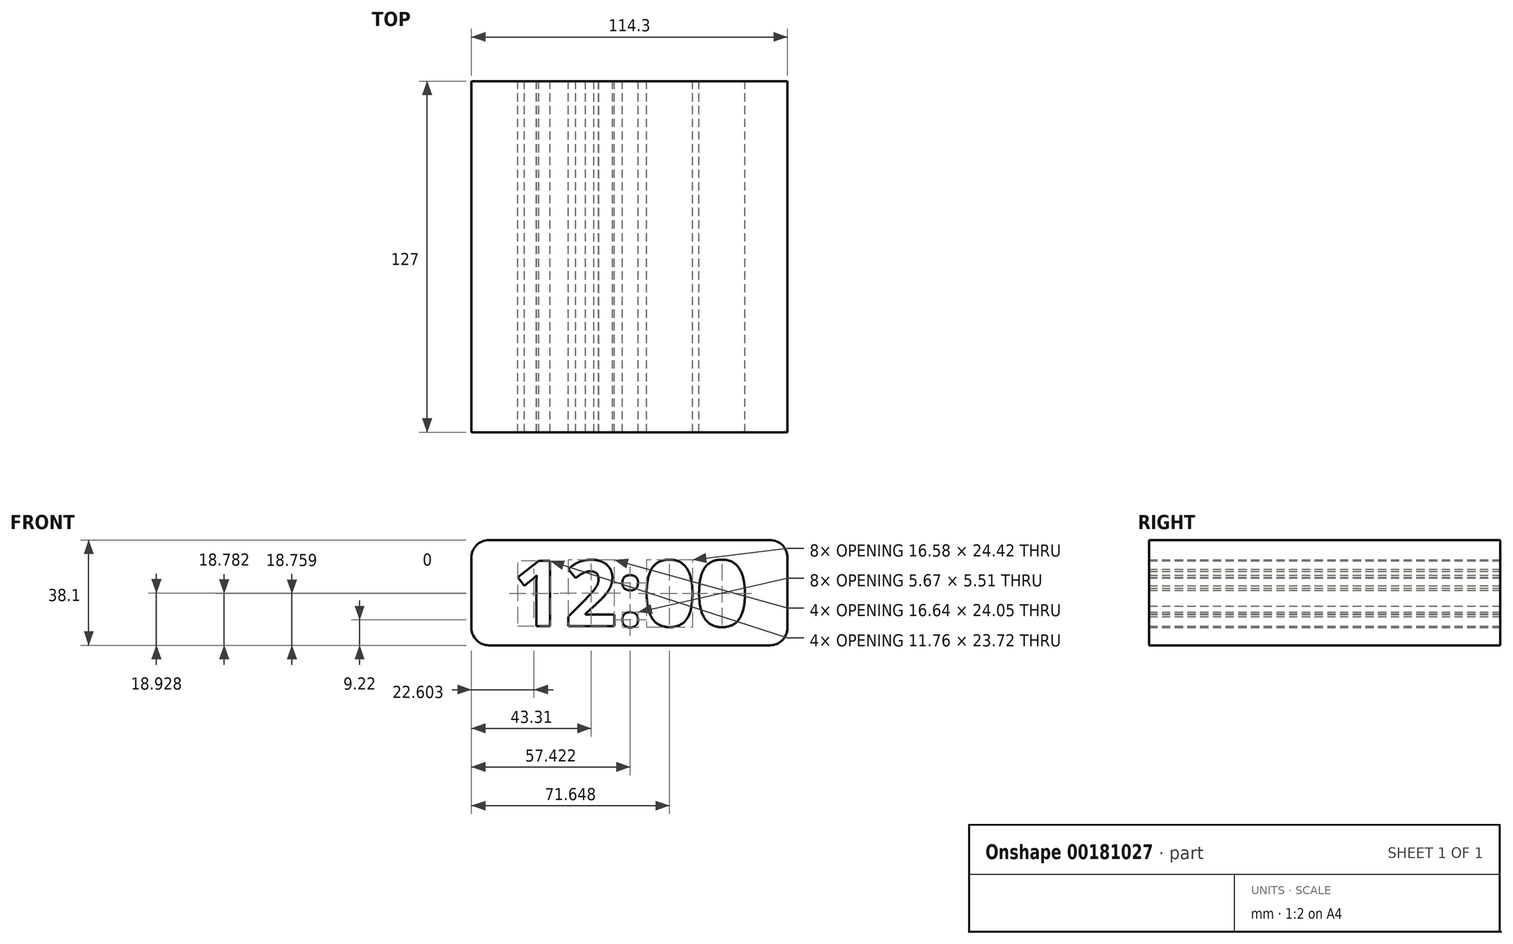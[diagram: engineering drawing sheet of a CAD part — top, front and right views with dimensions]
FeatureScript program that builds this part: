
annotation { "Feature Type Name" : "Feature", "Feature Type Description" : "" }
export const myFeature = defineFeature(function(context is Context, id is Id, definition is map)
    precondition{}
    {
        {
            var Q0;
            Q0=qCreatedBy(makeId("Front.planeOp"),FACE);
            var sketch = newSketch(context, id + "F0", { "sketchPlane" : qUnion([Q0])});
            skLineSegment(sketch, "E0.bottom", {"start": v(50.8, 19.05) * mm, "end": v(-50.8, 19.05) * mm});
            skLineSegment(sketch, "E0.top", {"start": v(50.8, -19.05) * mm, "end": v(-50.8, -19.05) * mm});
            skLineSegment(sketch, "E0.left", {"start": v(57.15, 12.7) * mm, "end": v(57.15, -12.7) * mm});
            skLineSegment(sketch, "E0.right", {"start": v(-57.15, 12.7) * mm, "end": v(-57.15, -12.7) * mm});
            skPoint(sketch, "E0.middle", {"position": v(0, 0) * mm});
            skText(sketch, "E1", { "text": "12:00", "fontName": "OpenSans-Bold.ttf"});
            skPoint(sketch, "E2.visualSharp", {"position": v(-57.15, 19.05) * mm});
            skArc(sketch, "E2.filletArc", {"start": v(-50.8, 19.05) * mm, "mid": v(-55.3, 17.2) * mm, "end": v(-57.15, 12.7) * mm});
            skPoint(sketch, "E3.visualSharp", {"position": v(-57.15, -19.05) * mm});
            skArc(sketch, "E3.filletArc", {"start": v(-57.15, -12.7) * mm, "mid": v(-55.3, -17.2) * mm, "end": v(-50.8, -19.05) * mm});
            skPoint(sketch, "E4.visualSharp", {"position": v(57.15, -19.05) * mm});
            skArc(sketch, "E4.filletArc", {"start": v(50.8, -19.05) * mm, "mid": v(55.3, -17.2) * mm, "end": v(57.15, -12.7) * mm});
            skPoint(sketch, "E5.visualSharp", {"position": v(57.15, 19.05) * mm});
            skArc(sketch, "E5.filletArc", {"start": v(57.15, 12.7) * mm, "mid": v(55.3, 17.2) * mm, "end": v(50.8, 19.05) * mm});
            const initialGuessF0  = {"E1": [-0.04239, -0.01215, 1, 0, 0.02392]};
            skSetInitialGuess(sketch, initialGuessF0);
            skSolve(sketch);
        }
        {
            var Q0;
            Q0=makeQuery(id+"F0.imprint","IMPRINT",FACE,{"disambiguationData":[TD([[makeQuery(id+"F0.imprint","IMPRINT",EDGE,{"derivedFrom":sQuery(id+"F0.wireOp",EDGE,"E0.bottom")}),1.0]])]});
            extrude(context, id + "F1", {"entities" : qUnion([Q0]), "depth" : 127 * mm});
        }
    });
